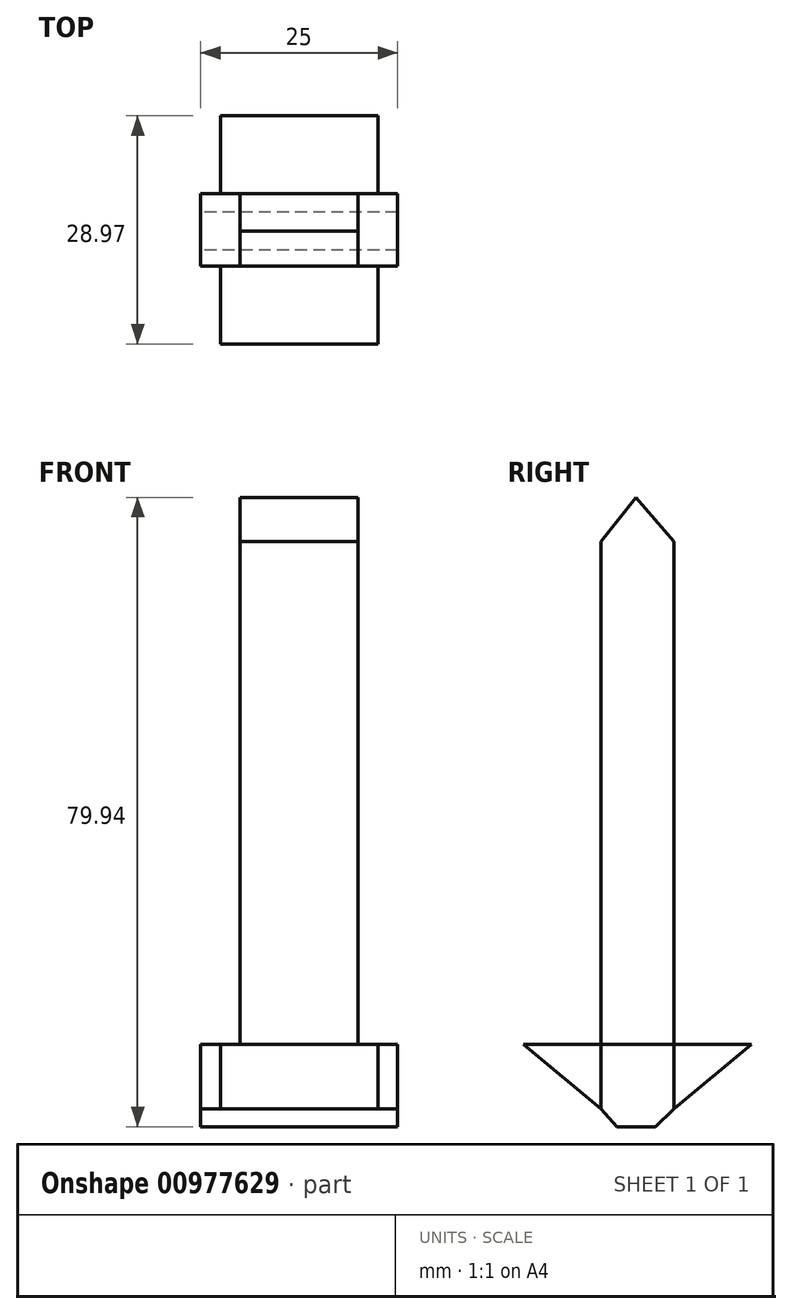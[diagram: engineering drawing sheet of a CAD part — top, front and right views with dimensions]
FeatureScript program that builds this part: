
annotation { "Feature Type Name" : "Feature", "Feature Type Description" : "" }
export const myFeature = defineFeature(function(context is Context, id is Id, definition is map)
    precondition{}
    {
        {
            var Q0;
            Q0=qCreatedBy(makeId("Right.planeOp"),FACE);
            var sketch = newSketch(context, id + "F0", { "sketchPlane" : qUnion([Q0])});
            skLineSegment(sketch, "E0.left", {"start": v(-4.44, 56.8) * mm, "end": v(-4.44, -15.31) * mm});
            skLineSegment(sketch, "E0.right", {"start": v(4.77, 56.8) * mm, "end": v(4.77, -15.31) * mm});
            skLineSegment(sketch, "E1", {"start": v(-4.44, 56.8) * mm, "end": v(0, 62.4) * mm});
            skLineSegment(sketch, "E2", {"start": v(4.77, 56.8) * mm, "end": v(0, 62.4) * mm});
            skLineSegment(sketch, "E3", {"start": v(-4.44, -15.31) * mm, "end": v(-14.32, -7.08) * mm});
            skLineSegment(sketch, "E4", {"start": v(-14.32, -7.08) * mm, "end": v(-4.44, -7.08) * mm});
            skLineSegment(sketch, "E5", {"start": v(4.77, -7.08) * mm, "end": v(4.77, -15.31) * mm});
            skLineSegment(sketch, "E6", {"start": v(4.77, -15.31) * mm, "end": v(14.65, -7.08) * mm});
            skLineSegment(sketch, "E7", {"start": v(14.65, -7.08) * mm, "end": v(4.77, -7.08) * mm});
            skLineSegment(sketch, "E8.top", {"start": v(0.16, -49.84) * mm, "end": v(2.42, -49.84) * mm});
            skLineSegment(sketch, "E8.right", {"start": v(2.42, -15.31) * mm, "end": v(2.42, -49.84) * mm});
            skLineSegment(sketch, "E9", {"start": v(0.16, -49.84) * mm, "end": v(-2.43, -49.84) * mm});
            skLineSegment(sketch, "E10", {"start": v(-2.43, -49.84) * mm, "end": v(-2.43, -15.31) * mm});
            skLineSegment(sketch, "E11", {"start": v(-4.44, -15.31) * mm, "end": v(-2.43, -17.55) * mm});
            skLineSegment(sketch, "E12", {"start": v(-2.43, -17.55) * mm, "end": v(2.42, -17.55) * mm});
            skLineSegment(sketch, "E13", {"start": v(2.42, -17.55) * mm, "end": v(4.77, -15.31) * mm});
            skArc(sketch, "E14", {"start": v(-2.43, -49.84) * mm, "mid": v(0, -58.5) * mm, "end": v(2.42, -49.84) * mm});
            skLineSegment(sketch, "E15", {"start": v(-4.44, -7.08) * mm, "end": v(4.77, -7.08) * mm});
            skSolve(sketch);
        }
        {
            var Q0;
            {var subQ0=sQuery(id+"F0.wireOp",EDGE,"E1");Q0=makeQuery(id+"F0.imprint","IMPRINT",FACE,{"disambiguationData":[TD([[makeQuery(id+"F0.imprint","IMPRINT",EDGE,{"derivedFrom":subQ0}),-1.0]])]});}
            extrude(context, id + "F1", {"entities" : qUnion([Q0]), "endBound" : BoundingType.SYMMETRIC, "depth" : 15 * mm, "offsetDistance" : 25 * mm});
        }
        {
            var Q0;
            {var subQ0=sQuery(id+"F0.wireOp",EDGE,"E3");Q0=makeQuery(id+"F0.imprint","IMPRINT",FACE,{"disambiguationData":[TD([[makeQuery(id+"F0.imprint","IMPRINT",EDGE,{"derivedFrom":subQ0}),-1.0]])]});}
            var Q1;
            {var subQ0=sQuery(id+"F0.wireOp",EDGE,"E6");Q1=makeQuery(id+"F0.imprint","IMPRINT",FACE,{"disambiguationData":[TD([[makeQuery(id+"F0.imprint","IMPRINT",EDGE,{"derivedFrom":subQ0}),1.0]])]});}
            extrude(context, id + "F2", {"entities" : qUnion([Q0, Q1]), "endBound" : BoundingType.SYMMETRIC, "depth" : 20 * mm, "offsetDistance" : 25 * mm});
        }
        {
            var Q0;
            {var subQ0=sQuery(id+"F0.wireOp",EDGE,"E11");Q0=makeQuery(id+"F0.imprint","IMPRINT",FACE,{"disambiguationData":[TD([[makeQuery(id+"F0.imprint","IMPRINT",EDGE,{"derivedFrom":subQ0}),1.0]])]});}
            extrude(context, id + "F3", {"entities" : qUnion([Q0]), "endBound" : BoundingType.SYMMETRIC, "depth" : 25 * mm, "offsetDistance" : 25 * mm});
        }
    });
